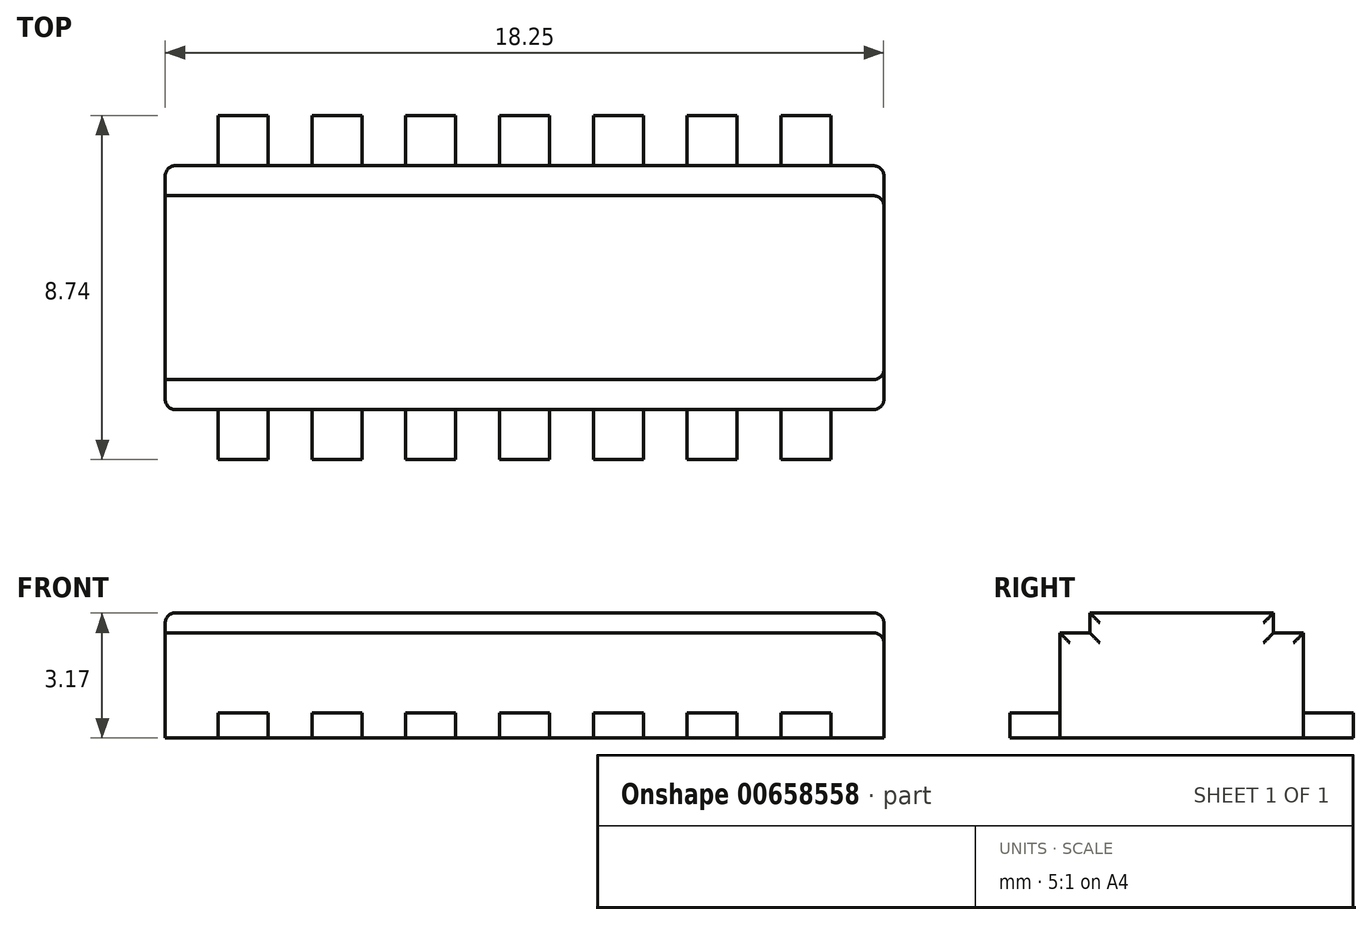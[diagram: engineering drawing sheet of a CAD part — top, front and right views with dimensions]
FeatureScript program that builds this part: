
annotation { "Feature Type Name" : "Feature", "Feature Type Description" : "" }
export const myFeature = defineFeature(function(context is Context, id is Id, definition is map)
    precondition{}
    {
        {
            var Q0;
            Q0=qCreatedBy(makeId("Top.planeOp"),FACE);
            var sketch = newSketch(context, id + "F0", { "sketchPlane" : qUnion([Q0])});
            skLineSegment(sketch, "E0.bottom", {"start": v(-9.61, 3.7) * mm, "end": v(8.64, 3.7) * mm});
            skLineSegment(sketch, "E0.top", {"start": v(-9.61, -2.49) * mm, "end": v(8.64, -2.49) * mm});
            skLineSegment(sketch, "E0.left", {"start": v(-9.61, 3.7) * mm, "end": v(-9.61, -2.49) * mm});
            skLineSegment(sketch, "E0.right", {"start": v(8.64, 3.7) * mm, "end": v(8.64, -2.49) * mm});
            skSolve(sketch);
        }
        {
            var Q0;
            Q0 = qSketchRegion(id + "F0", true);
            extrude(context, id + "F1", {"entities" : qUnion([Q0]), "depth" : 3.17 * mm, "offsetDistance" : 25.4 * mm});
        }
        {
            var Q0;
            Q0=qCreatedBy(makeId("Top.planeOp"),FACE);
            var sketch = newSketch(context, id + "F2", { "sketchPlane" : qUnion([Q0])});
            skLineSegment(sketch, "E1.bottom", {"start": v(-8.27, 4.98) * mm, "end": v(-7, 4.98) * mm});
            skLineSegment(sketch, "E1.top", {"start": v(-8.27, 3.7) * mm, "end": v(-7, 3.7) * mm});
            skLineSegment(sketch, "E1.left", {"start": v(-8.27, 4.98) * mm, "end": v(-8.27, 3.7) * mm});
            skLineSegment(sketch, "E1.right", {"start": v(-7, 4.98) * mm, "end": v(-7, 3.7) * mm});
            skLineSegment(sketch, "E2.1.0.0", {"start": v(-4.61, 4.98) * mm, "end": v(-4.61, 3.7) * mm});
            skLineSegment(sketch, "E2.1.0.1", {"start": v(-5.88, 4.98) * mm, "end": v(-5.88, 3.7) * mm});
            skLineSegment(sketch, "E2.1.0.2", {"start": v(-5.88, 3.7) * mm, "end": v(-4.61, 3.7) * mm});
            skLineSegment(sketch, "E2.1.0.3", {"start": v(-5.88, 4.98) * mm, "end": v(-4.61, 4.98) * mm});
            skLineSegment(sketch, "E2.2.0.0", {"start": v(-2.23, 4.98) * mm, "end": v(-2.23, 3.7) * mm});
            skLineSegment(sketch, "E2.2.0.1", {"start": v(-3.5, 4.98) * mm, "end": v(-3.5, 3.7) * mm});
            skLineSegment(sketch, "E2.2.0.2", {"start": v(-3.5, 3.7) * mm, "end": v(-2.23, 3.7) * mm});
            skLineSegment(sketch, "E2.2.0.3", {"start": v(-3.5, 4.98) * mm, "end": v(-2.23, 4.98) * mm});
            skLineSegment(sketch, "E2.3.0.0", {"start": v(0.15, 4.98) * mm, "end": v(0.15, 3.7) * mm});
            skLineSegment(sketch, "E2.3.0.1", {"start": v(-1.12, 4.98) * mm, "end": v(-1.12, 3.7) * mm});
            skLineSegment(sketch, "E2.3.0.2", {"start": v(-1.12, 3.7) * mm, "end": v(0.15, 3.7) * mm});
            skLineSegment(sketch, "E2.3.0.3", {"start": v(-1.12, 4.98) * mm, "end": v(0.15, 4.98) * mm});
            skLineSegment(sketch, "E2.4.0.0", {"start": v(2.53, 4.98) * mm, "end": v(2.53, 3.7) * mm});
            skLineSegment(sketch, "E2.4.0.1", {"start": v(1.26, 4.98) * mm, "end": v(1.26, 3.7) * mm});
            skLineSegment(sketch, "E2.4.0.2", {"start": v(1.26, 3.7) * mm, "end": v(2.53, 3.7) * mm});
            skLineSegment(sketch, "E2.4.0.3", {"start": v(1.26, 4.98) * mm, "end": v(2.53, 4.98) * mm});
            skLineSegment(sketch, "E2.5.0.0", {"start": v(4.92, 4.98) * mm, "end": v(4.92, 3.7) * mm});
            skLineSegment(sketch, "E2.5.0.1", {"start": v(3.65, 4.98) * mm, "end": v(3.65, 3.7) * mm});
            skLineSegment(sketch, "E2.5.0.2", {"start": v(3.65, 3.7) * mm, "end": v(4.92, 3.7) * mm});
            skLineSegment(sketch, "E2.5.0.3", {"start": v(3.65, 4.98) * mm, "end": v(4.92, 4.98) * mm});
            skLineSegment(sketch, "E2.6.0.0", {"start": v(7.3, 4.98) * mm, "end": v(7.3, 3.7) * mm});
            skLineSegment(sketch, "E2.6.0.1", {"start": v(6.03, 4.98) * mm, "end": v(6.03, 3.7) * mm});
            skLineSegment(sketch, "E2.6.0.2", {"start": v(6.03, 3.7) * mm, "end": v(7.3, 3.7) * mm});
            skLineSegment(sketch, "E2.6.0.3", {"start": v(6.03, 4.98) * mm, "end": v(7.3, 4.98) * mm});
            skLineSegment(sketch, "E2.direction1", {"start": v(-8.27, 3.7) * mm, "end": v(-5.88, 3.7) * mm, "construction": true});
            skLineSegment(sketch, "E3.bottom", {"start": v(-8.27, -2.49) * mm, "end": v(-7, -2.49) * mm});
            skLineSegment(sketch, "E3.top", {"start": v(-8.27, -3.76) * mm, "end": v(-7, -3.76) * mm});
            skLineSegment(sketch, "E3.left", {"start": v(-8.27, -2.49) * mm, "end": v(-8.27, -3.76) * mm});
            skLineSegment(sketch, "E3.right", {"start": v(-7, -2.49) * mm, "end": v(-7, -3.76) * mm});
            skLineSegment(sketch, "E4.1.0.0", {"start": v(-5.88, -3.76) * mm, "end": v(-4.61, -3.76) * mm});
            skLineSegment(sketch, "E4.1.0.1", {"start": v(-5.88, -2.49) * mm, "end": v(-5.88, -3.76) * mm});
            skLineSegment(sketch, "E4.1.0.2", {"start": v(-5.88, -2.49) * mm, "end": v(-4.61, -2.49) * mm});
            skLineSegment(sketch, "E4.1.0.3", {"start": v(-4.61, -2.49) * mm, "end": v(-4.61, -3.76) * mm});
            skLineSegment(sketch, "E4.2.0.0", {"start": v(-3.5, -3.76) * mm, "end": v(-2.23, -3.76) * mm});
            skLineSegment(sketch, "E4.2.0.1", {"start": v(-3.5, -2.49) * mm, "end": v(-3.5, -3.76) * mm});
            skLineSegment(sketch, "E4.2.0.2", {"start": v(-3.5, -2.49) * mm, "end": v(-2.23, -2.49) * mm});
            skLineSegment(sketch, "E4.2.0.3", {"start": v(-2.23, -2.49) * mm, "end": v(-2.23, -3.76) * mm});
            skLineSegment(sketch, "E4.3.0.0", {"start": v(-1.12, -3.76) * mm, "end": v(0.15, -3.76) * mm});
            skLineSegment(sketch, "E4.3.0.1", {"start": v(-1.12, -2.49) * mm, "end": v(-1.12, -3.76) * mm});
            skLineSegment(sketch, "E4.3.0.2", {"start": v(-1.12, -2.49) * mm, "end": v(0.15, -2.49) * mm});
            skLineSegment(sketch, "E4.3.0.3", {"start": v(0.15, -2.49) * mm, "end": v(0.15, -3.76) * mm});
            skLineSegment(sketch, "E4.4.0.0", {"start": v(1.26, -3.76) * mm, "end": v(2.53, -3.76) * mm});
            skLineSegment(sketch, "E4.4.0.1", {"start": v(1.26, -2.49) * mm, "end": v(1.26, -3.76) * mm});
            skLineSegment(sketch, "E4.4.0.2", {"start": v(1.26, -2.49) * mm, "end": v(2.53, -2.49) * mm});
            skLineSegment(sketch, "E4.4.0.3", {"start": v(2.53, -2.49) * mm, "end": v(2.53, -3.76) * mm});
            skLineSegment(sketch, "E4.5.0.0", {"start": v(3.65, -3.76) * mm, "end": v(4.92, -3.76) * mm});
            skLineSegment(sketch, "E4.5.0.1", {"start": v(3.65, -2.49) * mm, "end": v(3.65, -3.76) * mm});
            skLineSegment(sketch, "E4.5.0.2", {"start": v(3.65, -2.49) * mm, "end": v(4.92, -2.49) * mm});
            skLineSegment(sketch, "E4.5.0.3", {"start": v(4.92, -2.49) * mm, "end": v(4.92, -3.76) * mm});
            skLineSegment(sketch, "E4.6.0.0", {"start": v(6.03, -3.76) * mm, "end": v(7.3, -3.76) * mm});
            skLineSegment(sketch, "E4.6.0.1", {"start": v(6.03, -2.49) * mm, "end": v(6.03, -3.76) * mm});
            skLineSegment(sketch, "E4.6.0.2", {"start": v(6.03, -2.49) * mm, "end": v(7.3, -2.49) * mm});
            skLineSegment(sketch, "E4.6.0.3", {"start": v(7.3, -2.49) * mm, "end": v(7.3, -3.76) * mm});
            skLineSegment(sketch, "E4.direction1", {"start": v(-8.27, -3.76) * mm, "end": v(-5.88, -3.76) * mm, "construction": true});
            skSolve(sketch);
        }
        {
            var Q0;
            Q0 = qSketchRegion(id + "F2", true);
            extrude(context, id + "F3", {"entities" : qUnion([Q0]), "operationType" : NewBodyOperationType.ADD, "depth" : 0.64 * mm, "offsetDistance" : 25.4 * mm});
        }
        {
            var Q0;
            Q0=makeQuery(id+"F1.opExtrude","SWEPT_FACE",FACE,{"disambiguationData":[OSD([sQuery(id+"F0.wireOp",EDGE,"E0.left")])]});
            var sketch = newSketch(context, id + "F4", { "sketchPlane" : qUnion([Q0])});
            skSolve(sketch);
        }
        {
            var Q0;
            {var subQ0=sQuery(id+"F0.wireOp",EDGE,"E0.left");Q0=makeQuery(id+"F4.imprint","IMPRINT",FACE,{"disambiguationData":[TD([[makeQuery(id+"F4.imprint","IMPRINT",EDGE,{"derivedFrom":makeQuery(id+"F1.opExtrude","CAP_EDGE",EDGE,{"disambiguationData":[OSD([subQ0])],"isStart":true})}),1.0]])]});}
            var sketch = newSketch(context, id + "F5", { "sketchPlane" : qUnion([Q0])});
            skLineSegment(sketch, "E5.bottom", {"start": v(-3.7, 3.18) * mm, "end": v(-2.94, 3.18) * mm});
            skLineSegment(sketch, "E5.top", {"start": v(-3.7, 2.67) * mm, "end": v(-2.94, 2.67) * mm});
            skLineSegment(sketch, "E5.left", {"start": v(-3.7, 3.18) * mm, "end": v(-3.7, 2.67) * mm});
            skLineSegment(sketch, "E5.right", {"start": v(-2.94, 3.18) * mm, "end": v(-2.94, 2.67) * mm});
            skLineSegment(sketch, "E6.bottom", {"start": v(2.49, 3.18) * mm, "end": v(1.72, 3.18) * mm});
            skLineSegment(sketch, "E6.top", {"start": v(2.49, 2.67) * mm, "end": v(1.72, 2.67) * mm});
            skLineSegment(sketch, "E6.left", {"start": v(2.49, 3.18) * mm, "end": v(2.49, 2.67) * mm});
            skLineSegment(sketch, "E6.right", {"start": v(1.72, 3.18) * mm, "end": v(1.72, 2.67) * mm});
            skSolve(sketch);
        }
        {
            var Q0;
            Q0 = qSketchRegion(id + "F5", true);
            extrude(context, id + "F6", {"entities" : qUnion([Q0]), "operationType" : NewBodyOperationType.REMOVE, "oppositeDirection" : true, "depth" : 25.4 * mm, "offsetDistance" : 25.4 * mm});
        }
        {
            var Q0;
            Q0=makeQuery(id+"F6.boolean.opBoolean","COPY",EDGE,{"derivedFrom":makeQuery(id+"F6.opExtrude","SWEPT_EDGE",EDGE,{"disambiguationData":[OSD([sQuery(id+"F0.wireOp",EDGE,"E0.bottom"),sQuery(id+"F0.wireOp",EDGE,"E0.left"),sQuery(id+"F5.wireOp",EDGE,"E5.top"),sQuery(id+"F5.wireOp",EDGE,"E5.left")])]})});
            var Q1;
            Q1=makeQuery(id+"F6.boolean.opBoolean","COPY",EDGE,{"derivedFrom":makeQuery(id+"F6.opExtrude","SWEPT_EDGE",EDGE,{"disambiguationData":[OSD([sQuery(id+"F0.wireOp",EDGE,"E0.left"),sQuery(id+"F5.wireOp",EDGE,"E5.bottom"),sQuery(id+"F5.wireOp",EDGE,"E5.right")])]})});
            var Q2;
            Q2=makeQuery(id+"F6.boolean.opBoolean","COPY",EDGE,{"derivedFrom":makeQuery(id+"F6.opExtrude","SWEPT_EDGE",EDGE,{"disambiguationData":[OSD([sQuery(id+"F0.wireOp",EDGE,"E0.left"),sQuery(id+"F5.wireOp",EDGE,"E6.bottom"),sQuery(id+"F5.wireOp",EDGE,"E6.right")])]})});
            var Q3;
            Q3=makeQuery(id+"F6.boolean.opBoolean","COPY",EDGE,{"derivedFrom":makeQuery(id+"F6.opExtrude","SWEPT_EDGE",EDGE,{"disambiguationData":[OSD([sQuery(id+"F0.wireOp",EDGE,"E0.top"),sQuery(id+"F0.wireOp",EDGE,"E0.left"),sQuery(id+"F5.wireOp",EDGE,"E6.top"),sQuery(id+"F5.wireOp",EDGE,"E6.left")])]})});
            var Q4;
            Q4=makeQuery(id+"F1.opExtrude","CAP_EDGE",EDGE,{"disambiguationData":[OSD([sQuery(id+"F0.wireOp",EDGE,"E0.left")])],"isStart":false});
            var Q5;
            Q5=makeQuery(id+"F6.boolean.opBoolean","COPY",EDGE,{"derivedFrom":makeQuery(id+"F6.opExtrude","CAP_EDGE",EDGE,{"disambiguationData":[OSD([sQuery(id+"F5.wireOp",EDGE,"E6.right")])],"isStart":true})});
            var Q6;
            Q6=makeQuery(id+"F6.boolean.opBoolean","COPY",EDGE,{"derivedFrom":makeQuery(id+"F6.opExtrude","CAP_EDGE",EDGE,{"disambiguationData":[OSD([sQuery(id+"F5.wireOp",EDGE,"E6.top")])],"isStart":true})});
            var Q7;
            Q7=makeQuery(id+"F1.opExtrude","SWEPT_EDGE",EDGE,{"disambiguationData":[OSD([sQuery(id+"F0.wireOp",EDGE,"E0.top"),sQuery(id+"F0.wireOp",EDGE,"E0.left")])]});
            var Q8;
            Q8=makeQuery(id+"F6.boolean.opBoolean","COPY",EDGE,{"derivedFrom":makeQuery(id+"F6.opExtrude","CAP_EDGE",EDGE,{"disambiguationData":[OSD([sQuery(id+"F5.wireOp",EDGE,"E5.top")])],"isStart":true})});
            var Q9;
            Q9=makeQuery(id+"F6.boolean.opBoolean","COPY",EDGE,{"derivedFrom":makeQuery(id+"F6.opExtrude","CAP_EDGE",EDGE,{"disambiguationData":[OSD([sQuery(id+"F5.wireOp",EDGE,"E5.right")])],"isStart":true})});
            var Q10;
            Q10=makeQuery(id+"F1.opExtrude","SWEPT_EDGE",EDGE,{"disambiguationData":[OSD([sQuery(id+"F0.wireOp",EDGE,"E0.bottom"),sQuery(id+"F0.wireOp",EDGE,"E0.left")])]});
            var Q11;
            Q11=makeQuery(id+"F1.opExtrude","SWEPT_EDGE",EDGE,{"disambiguationData":[OSD([sQuery(id+"F0.wireOp",EDGE,"E0.top"),sQuery(id+"F0.wireOp",EDGE,"E0.right")])]});
            var Q12;
            Q12=makeQuery(id+"F6.boolean.opBoolean","INTERSECT",EDGE,{"derivedFrom":[makeQuery(id+"F1.opExtrude","SWEPT_FACE",FACE,{"disambiguationData":[OSD([sQuery(id+"F0.wireOp",EDGE,"E0.right")])]}),makeQuery(id+"F6.opExtrude","SWEPT_FACE",FACE,{"disambiguationData":[OSD([sQuery(id+"F5.wireOp",EDGE,"E6.top")])]})]});
            var Q13;
            Q13=makeQuery(id+"F6.boolean.opBoolean","INTERSECT",EDGE,{"derivedFrom":[makeQuery(id+"F1.opExtrude","SWEPT_FACE",FACE,{"disambiguationData":[OSD([sQuery(id+"F0.wireOp",EDGE,"E0.right")])]}),makeQuery(id+"F6.opExtrude","SWEPT_FACE",FACE,{"disambiguationData":[OSD([sQuery(id+"F5.wireOp",EDGE,"E6.right")])]})]});
            var Q14;
            Q14=makeQuery(id+"F1.opExtrude","CAP_EDGE",EDGE,{"disambiguationData":[OSD([sQuery(id+"F0.wireOp",EDGE,"E0.right")])],"isStart":false});
            var Q15;
            Q15=makeQuery(id+"F6.boolean.opBoolean","INTERSECT",EDGE,{"derivedFrom":[makeQuery(id+"F1.opExtrude","SWEPT_FACE",FACE,{"disambiguationData":[OSD([sQuery(id+"F0.wireOp",EDGE,"E0.right")])]}),makeQuery(id+"F6.opExtrude","SWEPT_FACE",FACE,{"disambiguationData":[OSD([sQuery(id+"F5.wireOp",EDGE,"E5.right")])]})]});
            var Q16;
            Q16=makeQuery(id+"F6.boolean.opBoolean","INTERSECT",EDGE,{"derivedFrom":[makeQuery(id+"F1.opExtrude","SWEPT_FACE",FACE,{"disambiguationData":[OSD([sQuery(id+"F0.wireOp",EDGE,"E0.right")])]}),makeQuery(id+"F6.opExtrude","SWEPT_FACE",FACE,{"disambiguationData":[OSD([sQuery(id+"F5.wireOp",EDGE,"E5.top")])]})]});
            var Q17;
            Q17=makeQuery(id+"F1.opExtrude","SWEPT_EDGE",EDGE,{"disambiguationData":[OSD([sQuery(id+"F0.wireOp",EDGE,"E0.bottom"),sQuery(id+"F0.wireOp",EDGE,"E0.right")])]});
            fillet(context, id + "F7", {"entities" : qUnion([Q0, Q1, Q2, Q3, Q4, Q5, Q6, Q7, Q8, Q9, Q10, Q11, Q12, Q13, Q14, Q15, Q16, Q17]), "radius" : 0.25 * mm, "tangentPropagation" : true, "allowEdgeOverflow" : false});
        }
    });
